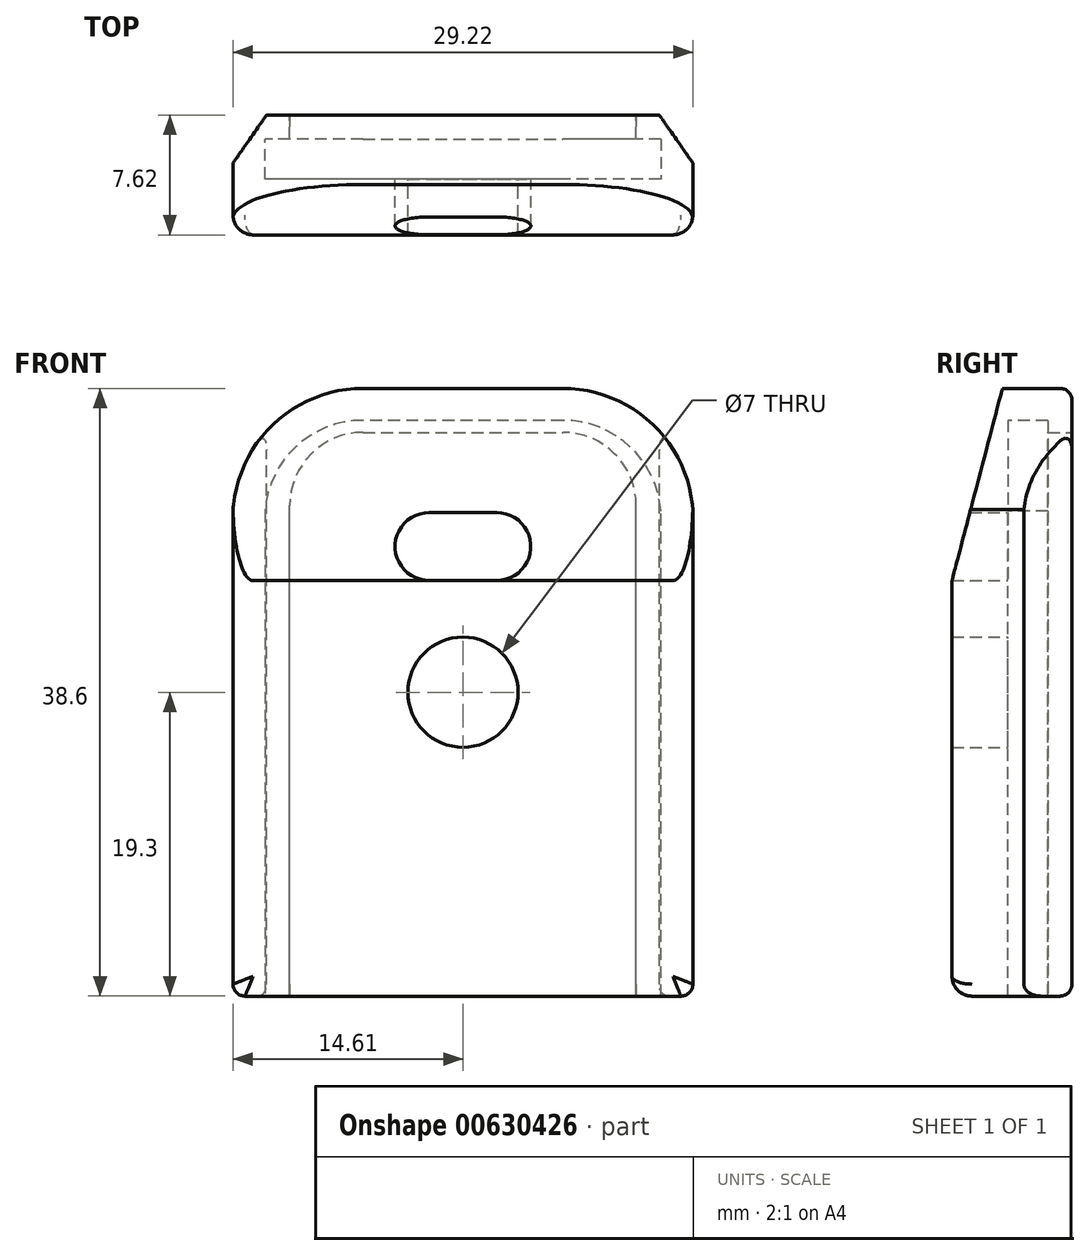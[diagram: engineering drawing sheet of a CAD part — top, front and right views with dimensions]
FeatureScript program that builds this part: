
annotation { "Feature Type Name" : "Feature", "Feature Type Description" : "" }
export const myFeature = defineFeature(function(context is Context, id is Id, definition is map)
    precondition{}
    {
        {
            var Q0;
            Q0=qCreatedBy(makeId("Front.planeOp"),FACE);
            var sketch = newSketch(context, id + "F0", { "sketchPlane" : qUnion([Q0])});
            skLineSegment(sketch, "E0.bottom", {"start": v(14.6, 19.3) * mm, "end": v(-14.6, 19.3) * mm});
            skLineSegment(sketch, "E0.top", {"start": v(14.6, -19.3) * mm, "end": v(-14.6, -19.3) * mm});
            skLineSegment(sketch, "E0.left", {"start": v(14.6, 19.3) * mm, "end": v(14.6, -19.3) * mm});
            skLineSegment(sketch, "E0.right", {"start": v(-14.6, 19.3) * mm, "end": v(-14.6, -19.3) * mm});
            skPoint(sketch, "E0.middle", {"position": v(0, 0) * mm});
            skPoint(sketch, "E1.endSnap0", {"position": v(0, 19.3) * mm});
            skLineSegment(sketch, "E2", {"start": v(0, 19.3) * mm, "end": v(6.35, 19.3) * mm, "construction": true});
            skLineSegment(sketch, "E3", {"start": v(0, 26.8) * mm, "end": v(0, -22.8) * mm, "construction": true});
            skPoint(sketch, "E3.endSnap0", {"position": v(0, -19.3) * mm});
            skLineSegment(sketch, "E4.MirrorCS", {"start": v(0, 19.3) * mm, "end": v(-6.35, 19.3) * mm, "construction": true});
            skArc(sketch, "E5", {"start": v(-6.35, 19.3) * mm, "mid": v(-12.4, 16.68) * mm, "end": v(-14.6, 10.46) * mm});
            skArc(sketch, "E6.MirrorCS", {"start": v(6.35, 19.3) * mm, "mid": v(12.4, 16.68) * mm, "end": v(14.6, 10.46) * mm});
            skSolve(sketch);
        }
        {
            var Q0;
            {var subQ4=sQuery(id+"F0.wireOp",EDGE,"E0.top");Q0=makeQuery(id+"F0.imprint","IMPRINT",FACE,{"disambiguationData":[TD([[makeQuery(id+"F0.imprint","IMPRINT",EDGE,{"derivedFrom":subQ4}),-1.0]])]});}
            extrude(context, id + "F1", {"entities" : qUnion([Q0]), "depth" : 7.62 * mm, "offsetDistance" : 25.4 * mm});
        }
        {
            var Q0;
            Q0=qCreatedBy(makeId("Front.planeOp"),FACE);
            var sketch = newSketch(context, id + "F2", { "sketchPlane" : qUnion([Q0])});
            skLineSegment(sketch, "E7", {"start": v(0, 19.42) * mm, "end": v(0, 11.42) * mm, "construction": true});
            skLineSegment(sketch, "E8.top", {"start": v(0, 11.42) * mm, "end": v(-2.16, 11.42) * mm});
            skLineSegment(sketch, "E8.left", {"start": v(0, 9.26) * mm, "end": v(0, 11.42) * mm});
            skLineSegment(sketch, "E9.MirrorCS", {"start": v(0, 7.1) * mm, "end": v(-2.16, 7.1) * mm});
            skLineSegment(sketch, "E10.MirrorCS", {"start": v(0, 11.42) * mm, "end": v(2.16, 11.42) * mm});
            skLineSegment(sketch, "E11.MirrorCS", {"start": v(0, 7.1) * mm, "end": v(2.16, 7.1) * mm});
            skArc(sketch, "E12", {"start": v(-2.16, 11.42) * mm, "mid": v(-4.32, 9.26) * mm, "end": v(-2.16, 7.1) * mm});
            skLineSegment(sketch, "E13", {"start": v(2.16, 9.26) * mm, "end": v(8.2, 9.26) * mm, "construction": true});
            skArc(sketch, "E14", {"start": v(2.16, 7.1) * mm, "mid": v(4.32, 9.26) * mm, "end": v(2.16, 11.42) * mm});
            skPoint(sketch, "E15.orphan", {"position": v(-4, 11.42) * mm});
            skPoint(sketch, "E16.orphan", {"position": v(-4, 9.26) * mm});
            skPoint(sketch, "E17.orphan", {"position": v(4, 11.42) * mm});
            skPoint(sketch, "E18.MirrorCS.start.orphan", {"position": v(4, 9.26) * mm});
            skPoint(sketch, "E19.MirrorCS.end.orphan", {"position": v(4, 7.1) * mm});
            skPoint(sketch, "E20.MirrorCS.end.orphan", {"position": v(-4, 7.1) * mm});
            skLineSegment(sketch, "E21.0", {"start": v(14.6, -19.3) * mm, "end": v(-14.6, -19.3) * mm, "construction": true});
            skCircle(sketch, "E22", {"center": v(0, 0) * mm, "radius": 3.5 * mm});
            skSolve(sketch);
        }
        {
            var Q0;
            Q0=qSketchRegion(id+"F2",true);
            extrude(context, id + "F3", {"entities" : qUnion([Q0]), "operationType" : NewBodyOperationType.REMOVE, "depth" : 25.4 * mm, "offsetDistance" : 25.4 * mm});
        }
        {
            var Q0;
            Q0=qCreatedBy(makeId("Front.planeOp"),FACE);
            var sketch = newSketch(context, id + "F4", { "sketchPlane" : qUnion([Q0])});
            skLineSegment(sketch, "E23.bottom", {"start": v(11, -21.12) * mm, "end": v(-11, -21.12) * mm});
            skLineSegment(sketch, "E23.left", {"start": v(11, -21.12) * mm, "end": v(11, -1.93) * mm});
            skLineSegment(sketch, "E23.right", {"start": v(-11, -21.12) * mm, "end": v(-11, -1.93) * mm});
            skPoint(sketch, "E23.middle", {"position": v(0, 0) * mm});
            skLineSegment(sketch, "E24", {"start": v(5.3, 16.5) * mm, "end": v(-6.35, 16.5) * mm});
            skLineSegment(sketch, "E25", {"start": v(-6.35, 16.5) * mm, "end": v(6.35, 16.5) * mm});
            skPoint(sketch, "E26.orphan", {"position": v(11, 21.12) * mm});
            skPoint(sketch, "E27.orphan", {"position": v(-11, 21.12) * mm});
            skLineSegment(sketch, "E28", {"start": v(0, 16.5) * mm, "end": v(6.35, 16.5) * mm, "construction": true});
            skLineSegment(sketch, "E29.MirrorCS", {"start": v(0, 16.5) * mm, "end": v(-6.35, 16.5) * mm, "construction": true});
            skArc(sketch, "E30", {"start": v(11, 11.86) * mm, "mid": v(9.64, 15.14) * mm, "end": v(6.35, 16.5) * mm});
            skArc(sketch, "E31.MirrorCS", {"start": v(-11, 11.86) * mm, "mid": v(-9.64, 15.14) * mm, "end": v(-6.35, 16.5) * mm});
            skPoint(sketch, "E32.orphan", {"position": v(11, 16.5) * mm});
            skPoint(sketch, "E33.orphan", {"position": v(-11, 16.5) * mm});
            skLineSegment(sketch, "E34.trimOffspring", {"start": v(-11, 2.96) * mm, "end": v(-11, 11.86) * mm});
            skLineSegment(sketch, "E35.trimOffspring", {"start": v(11, 2.96) * mm, "end": v(11, 11.86) * mm});
            skLineSegment(sketch, "E36", {"start": v(11, 2.96) * mm, "end": v(11, -1.93) * mm});
            skLineSegment(sketch, "E37", {"start": v(-11, 2.96) * mm, "end": v(-11, -1.93) * mm});
            skPoint(sketch, "E38.MirrorCS.start.orphan", {"position": v(13.08, 2.37) * mm});
            skPoint(sketch, "E39.MirrorCS.start.orphan", {"position": v(13.08, -1.93) * mm});
            skPoint(sketch, "E40.end.orphan", {"position": v(-13.08, 2.37) * mm});
            skPoint(sketch, "E41.end.orphan", {"position": v(-13.08, -1.93) * mm});
            skSolve(sketch);
        }
        {
            var Q0;
            Q0=qSketchRegion(id+"F4",true);
            extrude(context, id + "F5", {"entities" : qUnion([Q0]), "operationType" : NewBodyOperationType.REMOVE, "depth" : 4.06 * mm, "offsetDistance" : 25.4 * mm});
        }
        {
            var Q0;
            Q0=qCreatedBy(makeId("Top.planeOp"),FACE);
            var sketch = newSketch(context, id + "F6", { "sketchPlane" : qUnion([Q0])});
            skLineSegment(sketch, "E42.bottom", {"start": v(-11.75, -4.06) * mm, "end": v(11.75, -4.06) * mm});
            skLineSegment(sketch, "E42.top", {"start": v(-11.75, -1.56) * mm, "end": v(11.75, -1.56) * mm});
            skLineSegment(sketch, "E42.left", {"start": v(-11.75, -4.06) * mm, "end": v(-11.75, -1.56) * mm});
            skLineSegment(sketch, "E42.right", {"start": v(11.75, -4.06) * mm, "end": v(11.75, -1.56) * mm});
            skPoint(sketch, "E42.middle", {"position": v(0, -2.8) * mm});
            skSolve(sketch);
        }
        {
            var Q0;
            Q0=makeQuery(id+"F1.opExtrude","CAP_EDGE",EDGE,{"disambiguationData":[OSD([sQuery(id+"F0.wireOp",EDGE,"E0.left")])],"isStart":false});
            var Q1;
            Q1=makeQuery(id+"F1.opExtrude","CAP_EDGE",EDGE,{"disambiguationData":[OSD([sQuery(id+"F0.wireOp",EDGE,"E6.MirrorCS")])],"isStart":false});
            var Q2;
            Q2=makeQuery(id+"F1.opExtrude","CAP_EDGE",EDGE,{"disambiguationData":[OSD([sQuery(id+"F0.wireOp",EDGE,"E0.bottom")])],"isStart":false});
            var Q3;
            Q3=makeQuery(id+"F1.opExtrude","CAP_EDGE",EDGE,{"disambiguationData":[OSD([sQuery(id+"F0.wireOp",EDGE,"E5")])],"isStart":false});
            var Q4;
            Q4=makeQuery(id+"F1.opExtrude","CAP_EDGE",EDGE,{"disambiguationData":[OSD([sQuery(id+"F0.wireOp",EDGE,"E0.right")])],"isStart":false});
            var Q5;
            Q5=makeQuery(id+"F1.opExtrude","CAP_EDGE",EDGE,{"disambiguationData":[OSD([sQuery(id+"F0.wireOp",EDGE,"E0.top")])],"isStart":false});
            fillet(context, id + "F7", {"entities" : qUnion([Q0, Q1, Q2, Q3, Q4, Q5]), "radius" : 1.27 * mm, "tangentPropagation" : true, "allowEdgeOverflow" : false});
        }
        {
            var Q0;
            Q0=makeQuery(id+"F1.opExtrude","SWEPT_EDGE",EDGE,{"disambiguationData":[OSD([sQuery(id+"F0.wireOp",EDGE,"E0.top"),sQuery(id+"F0.wireOp",EDGE,"E0.left")])]});
            var Q1;
            Q1=makeQuery(id+"F1.opExtrude","SWEPT_EDGE",EDGE,{"disambiguationData":[OSD([sQuery(id+"F0.wireOp",EDGE,"E0.top"),sQuery(id+"F0.wireOp",EDGE,"E0.right")])]});
            fillet(context, id + "F8", {"entities" : qUnion([Q0, Q1]), "radius" : 0.76 * mm, "tangentPropagation" : true, "allowEdgeOverflow" : false});
        }
        {
            var Q0;
            Q0=makeQuery(id+"F1.opExtrude","CAP_EDGE",EDGE,{"disambiguationData":[OSD([sQuery(id+"F0.wireOp",EDGE,"E0.left")])],"isStart":true});
            var Q1;
            Q1=makeQuery(id+"F1.opExtrude","CAP_EDGE",EDGE,{"disambiguationData":[OSD([sQuery(id+"F0.wireOp",EDGE,"E6.MirrorCS")])],"isStart":true});
            var Q2;
            Q2=makeQuery(id+"F1.opExtrude","CAP_EDGE",EDGE,{"disambiguationData":[OSD([sQuery(id+"F0.wireOp",EDGE,"E0.bottom")])],"isStart":true});
            var Q3;
            Q3=makeQuery(id+"F1.opExtrude","CAP_EDGE",EDGE,{"disambiguationData":[OSD([sQuery(id+"F0.wireOp",EDGE,"E5")])],"isStart":true});
            var Q4;
            Q4=makeQuery(id+"F1.opExtrude","CAP_EDGE",EDGE,{"disambiguationData":[OSD([sQuery(id+"F0.wireOp",EDGE,"E0.right")])],"isStart":true});
            fillet(context, id + "F9", {"entities" : qUnion([Q0, Q1, Q2, Q3, Q4]), "radius" : 0.76 * mm, "tangentPropagation" : true, "allowEdgeOverflow" : false});
        }
        {
            var Q0;
            Q0=makeQuery(id+"F1.opExtrude","CAP_FACE",FACE,{"disambiguationData":[OSD([sQuery(id+"F0.wireOp",EDGE,"E0.bottom"),sQuery(id+"F0.wireOp",EDGE,"E0.top"),sQuery(id+"F0.wireOp",EDGE,"E0.left"),sQuery(id+"F0.wireOp",EDGE,"E0.right"),sQuery(id+"F0.wireOp",EDGE,"E5"),sQuery(id+"F0.wireOp",EDGE,"E6.MirrorCS")])],"isStart":false});
            var sketch = newSketch(context, id + "F10", { "sketchPlane" : qUnion([Q0])});
            skLineSegment(sketch, "E43.0", {"start": v(-12.57, 11.52) * mm, "end": v(-12.57, -18.03) * mm});
            skLineSegment(sketch, "E43.1", {"start": v(12.57, -18.03) * mm, "end": v(12.57, 11.52) * mm});
            skArc(sketch, "E43.2", {"start": v(12.57, 11.52) * mm, "mid": v(10.59, 15.62) * mm, "end": v(6.35, 17.27) * mm});
            skLineSegment(sketch, "E43.3", {"start": v(6.35, 17.27) * mm, "end": v(-6.35, 17.27) * mm});
            skArc(sketch, "E43.4", {"start": v(-6.35, 17.27) * mm, "mid": v(-10.59, 15.62) * mm, "end": v(-12.57, 11.52) * mm});
            skLineSegment(sketch, "E44", {"start": v(12.57, -18.03) * mm, "end": v(12.57, -26.18) * mm});
            skLineSegment(sketch, "E45", {"start": v(12.57, -26.18) * mm, "end": v(-12.57, -26.18) * mm});
            skLineSegment(sketch, "E46", {"start": v(-12.57, -26.18) * mm, "end": v(-12.57, -18.03) * mm});
            skSolve(sketch);
        }
        {
            var Q0;
            {var subQ1=sQuery(id+"F10.wireOp",EDGE,"E43.0");Q0=makeQuery(id+"F10.imprint","IMPRINT",FACE,{"disambiguationData":[TD([[makeQuery(id+"F10.imprint","IMPRINT",EDGE,{"derivedFrom":subQ1}),1.0]])]});}
            var Q1;
            {var subQ0=sQuery(id+"F10.wireOp",EDGE,"E44");Q1=makeQuery(id+"F10.imprint","IMPRINT",FACE,{"disambiguationData":[TD([[makeQuery(id+"F10.imprint","IMPRINT",EDGE,{"derivedFrom":subQ0}),-1.0]])]});}
            extrude(context, id + "F11", {"entities" : qUnion([Q0, Q1]), "operationType" : NewBodyOperationType.REMOVE, "oppositeDirection" : true, "depth" : 6.1 * mm, "offsetDistance" : 25.4 * mm, "hasSecondDirection" : true, "secondDirectionOppositeDirection" : true, "secondDirectionDepth" : 3.56 * mm});
        }
        {
            var Q0;
            Q0=qCreatedBy(makeId("Top.planeOp"),FACE);
            var sketch = newSketch(context, id + "F12", { "sketchPlane" : qUnion([Q0])});
            skLineSegment(sketch, "E47", {"start": v(0, -34.55) * mm, "end": v(0, 19.64) * mm, "construction": true});
            skLineSegment(sketch, "E48", {"start": v(-16.37, -5.58) * mm, "end": v(-9.37, 4.42) * mm});
            skLineSegment(sketch, "E49", {"start": v(-9.37, 4.42) * mm, "end": v(-16.94, 4.42) * mm});
            skLineSegment(sketch, "E50", {"start": v(-16.94, 4.42) * mm, "end": v(-16.37, -5.58) * mm});
            skLineSegment(sketch, "E51.MirrorCS", {"start": v(16.37, -5.58) * mm, "end": v(9.37, 4.42) * mm});
            skLineSegment(sketch, "E52.MirrorCS", {"start": v(9.37, 4.42) * mm, "end": v(16.94, 4.42) * mm});
            skLineSegment(sketch, "E53.MirrorCS", {"start": v(16.94, 4.42) * mm, "end": v(16.37, -5.58) * mm});
            skSolve(sketch);
        }
        {
            var Q0;
            Q0 = qSketchRegion(id + "F12", true);
            extrude(context, id + "F13", {"entities" : qUnion([Q0]), "operationType" : NewBodyOperationType.REMOVE, "endBound" : BoundingType.SYMMETRIC, "oppositeDirection" : true, "depth" : 80 * mm, "offsetDistance" : 25 * mm});
        }
        {
            var Q0;
            Q0=qCreatedBy(makeId("Right.planeOp"),FACE);
            var sketch = newSketch(context, id + "F14", { "sketchPlane" : qUnion([Q0])});
            skLineSegment(sketch, "E54", {"start": v(-11.67, -8.33) * mm, "end": v(-2.23, 27.63) * mm});
            skLineSegment(sketch, "E55", {"start": v(-14.6, 27.63) * mm, "end": v(-11.67, -8.33) * mm});
            skLineSegment(sketch, "E56", {"start": v(-14.6, 27.63) * mm, "end": v(-2.23, 27.63) * mm});
            skSolve(sketch);
        }
        {
            var Q0;
            Q0 = qSketchRegion(id + "F14", true);
            extrude(context, id + "F15", {"entities" : qUnion([Q0]), "operationType" : NewBodyOperationType.REMOVE, "endBound" : BoundingType.SYMMETRIC, "depth" : 50 * mm, "offsetDistance" : 25 * mm});
        }
    });
